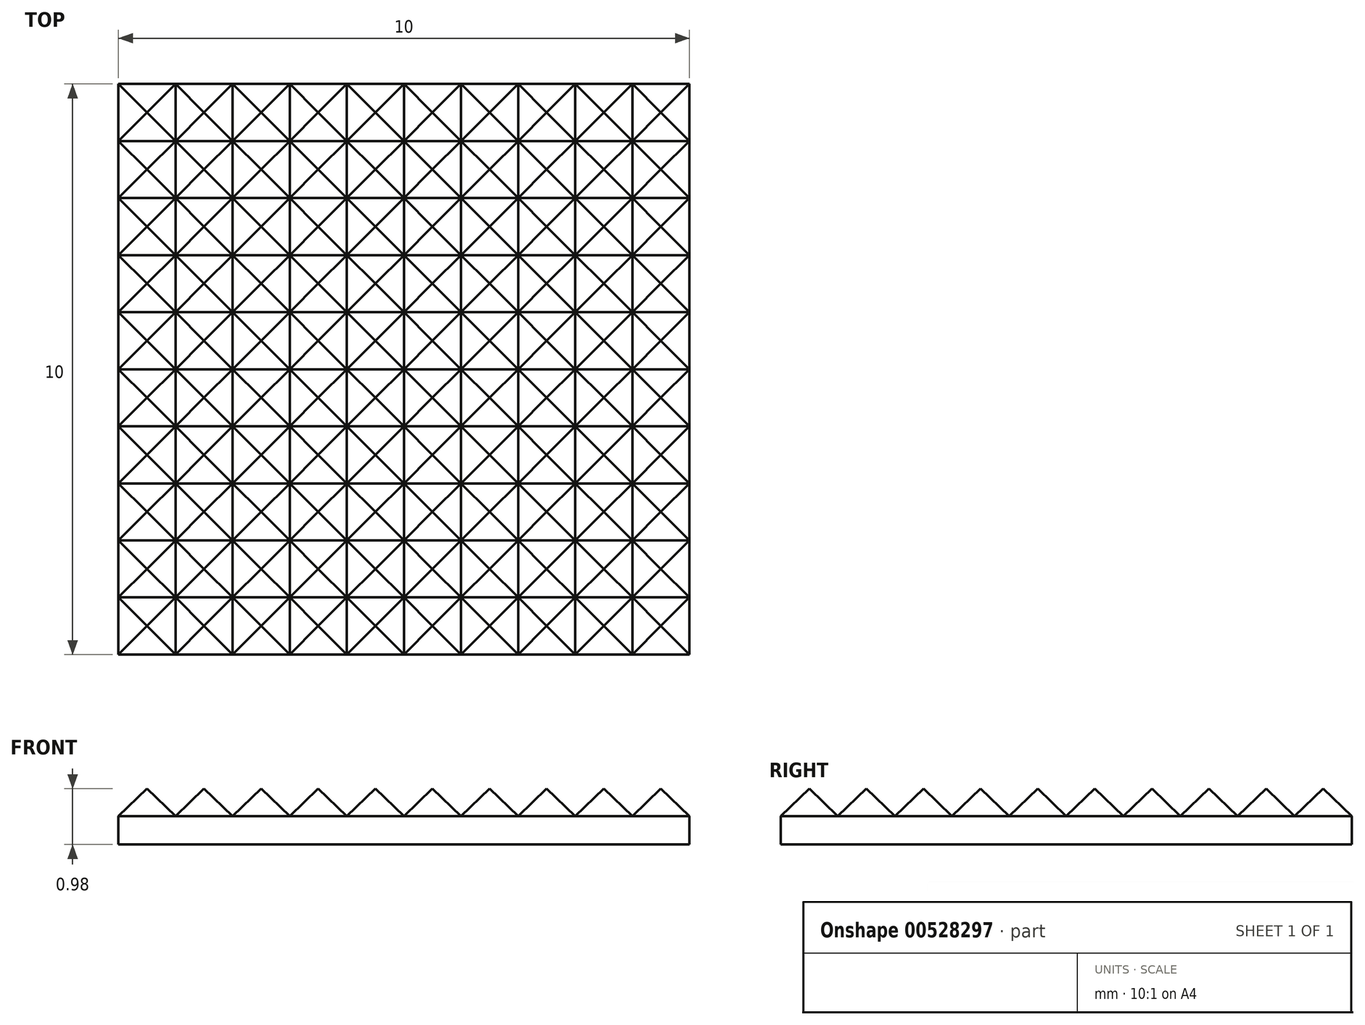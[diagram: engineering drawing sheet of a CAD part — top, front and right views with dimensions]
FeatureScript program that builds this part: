
annotation { "Feature Type Name" : "Feature", "Feature Type Description" : "" }
export const myFeature = defineFeature(function(context is Context, id is Id, definition is map)
    precondition{}
    {
        {
            var Q0;
            Q0=qCreatedBy(makeId("Top.planeOp"),FACE);
            var sketch = newSketch(context, id + "F0", { "sketchPlane" : qUnion([Q0])});
            skLineSegment(sketch, "E0.bottom", {"start": v(0, 0) * mm, "end": v(10, 0) * mm});
            skLineSegment(sketch, "E0.top", {"start": v(0, -10) * mm, "end": v(10, -10) * mm});
            skLineSegment(sketch, "E0.left", {"start": v(0, 0) * mm, "end": v(0, -10) * mm});
            skLineSegment(sketch, "E0.right", {"start": v(10, 0) * mm, "end": v(10, -10) * mm});
            skSolve(sketch);
        }
        {
            var Q0;
            Q0 = qSketchRegion(id + "F0", true);
            extrude(context, id + "F1", {"entities" : qUnion([Q0]), "depth" : 1 * mm, "offsetDistance" : 25 * mm});
        }
        {
            var Q0;
            Q0=makeQuery(id+"F1.opExtrude","SWEPT_FACE",FACE,{"disambiguationData":[OSD([sQuery(id+"F0.wireOp",EDGE,"E0.bottom")])]});
            var sketch = newSketch(context, id + "F2", { "sketchPlane" : qUnion([Q0])});
            skLineSegment(sketch, "E1", {"start": v(-10, 0.5) * mm, "end": v(0, 0.5) * mm});
            skLineSegment(sketch, "E2", {"start": v(0, 0.5) * mm, "end": v(-0.5, 0.98) * mm});
            skLineSegment(sketch, "E3", {"start": v(-0.5, 0.98) * mm, "end": v(-1, 0.5) * mm});
            skLineSegment(sketch, "E4.1.0.0", {"start": v(-1.5, 0.98) * mm, "end": v(-2, 0.5) * mm});
            skLineSegment(sketch, "E4.1.0.1", {"start": v(-1, 0.5) * mm, "end": v(-1.5, 0.98) * mm});
            skLineSegment(sketch, "E4.2.0.0", {"start": v(-2.5, 0.98) * mm, "end": v(-3, 0.5) * mm});
            skLineSegment(sketch, "E4.2.0.1", {"start": v(-2, 0.5) * mm, "end": v(-2.5, 0.98) * mm});
            skLineSegment(sketch, "E4.3.0.0", {"start": v(-3.5, 0.98) * mm, "end": v(-4, 0.5) * mm});
            skLineSegment(sketch, "E4.3.0.1", {"start": v(-3, 0.5) * mm, "end": v(-3.5, 0.98) * mm});
            skLineSegment(sketch, "E4.4.0.0", {"start": v(-4.5, 0.98) * mm, "end": v(-5, 0.5) * mm});
            skLineSegment(sketch, "E4.4.0.1", {"start": v(-4, 0.5) * mm, "end": v(-4.5, 0.98) * mm});
            skLineSegment(sketch, "E4.5.0.0", {"start": v(-5.5, 0.98) * mm, "end": v(-6, 0.5) * mm});
            skLineSegment(sketch, "E4.5.0.1", {"start": v(-5, 0.5) * mm, "end": v(-5.5, 0.98) * mm});
            skLineSegment(sketch, "E4.6.0.0", {"start": v(-6.5, 0.98) * mm, "end": v(-7, 0.5) * mm});
            skLineSegment(sketch, "E4.6.0.1", {"start": v(-6, 0.5) * mm, "end": v(-6.5, 0.98) * mm});
            skLineSegment(sketch, "E4.7.0.0", {"start": v(-7.5, 0.98) * mm, "end": v(-8, 0.5) * mm});
            skLineSegment(sketch, "E4.7.0.1", {"start": v(-7, 0.5) * mm, "end": v(-7.5, 0.98) * mm});
            skLineSegment(sketch, "E4.8.0.0", {"start": v(-8.5, 0.98) * mm, "end": v(-9, 0.5) * mm});
            skLineSegment(sketch, "E4.8.0.1", {"start": v(-8, 0.5) * mm, "end": v(-8.5, 0.98) * mm});
            skLineSegment(sketch, "E4.9.0.0", {"start": v(-9.5, 0.98) * mm, "end": v(-10, 0.5) * mm});
            skLineSegment(sketch, "E4.9.0.1", {"start": v(-9, 0.5) * mm, "end": v(-9.5, 0.98) * mm});
            skLineSegment(sketch, "E4.direction1", {"start": v(-1, 0.5) * mm, "end": v(-2, 0.5) * mm, "construction": true});
            skSolve(sketch);
        }
        {
            var Q0;
            Q0=makeQuery(id+"F1.opExtrude","SWEPT_FACE",FACE,{"disambiguationData":[OSD([sQuery(id+"F0.wireOp",EDGE,"E0.left")])]});
            var sketch = newSketch(context, id + "F3", { "sketchPlane" : qUnion([Q0])});
            skLineSegment(sketch, "E5", {"start": v(0, 0.5) * mm, "end": v(10, 0.5) * mm});
            skLineSegment(sketch, "E6", {"start": v(0, 0.5) * mm, "end": v(0.5, 0.98) * mm});
            skLineSegment(sketch, "E7", {"start": v(0.5, 0.98) * mm, "end": v(1, 0.5) * mm});
            skLineSegment(sketch, "E8.1.0.0", {"start": v(1, 0.5) * mm, "end": v(1.5, 0.98) * mm});
            skLineSegment(sketch, "E8.1.0.1", {"start": v(1.5, 0.98) * mm, "end": v(2, 0.5) * mm});
            skLineSegment(sketch, "E8.2.0.0", {"start": v(2, 0.5) * mm, "end": v(2.5, 0.98) * mm});
            skLineSegment(sketch, "E8.2.0.1", {"start": v(2.5, 0.98) * mm, "end": v(3, 0.5) * mm});
            skLineSegment(sketch, "E8.3.0.0", {"start": v(3, 0.5) * mm, "end": v(3.5, 0.98) * mm});
            skLineSegment(sketch, "E8.3.0.1", {"start": v(3.5, 0.98) * mm, "end": v(4, 0.5) * mm});
            skLineSegment(sketch, "E8.4.0.0", {"start": v(4, 0.5) * mm, "end": v(4.5, 0.98) * mm});
            skLineSegment(sketch, "E8.4.0.1", {"start": v(4.5, 0.98) * mm, "end": v(5, 0.5) * mm});
            skLineSegment(sketch, "E8.5.0.0", {"start": v(5, 0.5) * mm, "end": v(5.5, 0.98) * mm});
            skLineSegment(sketch, "E8.5.0.1", {"start": v(5.5, 0.98) * mm, "end": v(6, 0.5) * mm});
            skLineSegment(sketch, "E8.6.0.0", {"start": v(6, 0.5) * mm, "end": v(6.5, 0.98) * mm});
            skLineSegment(sketch, "E8.6.0.1", {"start": v(6.5, 0.98) * mm, "end": v(7, 0.5) * mm});
            skLineSegment(sketch, "E8.7.0.0", {"start": v(7, 0.5) * mm, "end": v(7.5, 0.98) * mm});
            skLineSegment(sketch, "E8.7.0.1", {"start": v(7.5, 0.98) * mm, "end": v(8, 0.5) * mm});
            skLineSegment(sketch, "E8.8.0.0", {"start": v(8, 0.5) * mm, "end": v(8.5, 0.98) * mm});
            skLineSegment(sketch, "E8.8.0.1", {"start": v(8.5, 0.98) * mm, "end": v(9, 0.5) * mm});
            skLineSegment(sketch, "E8.9.0.0", {"start": v(9, 0.5) * mm, "end": v(9.5, 0.98) * mm});
            skLineSegment(sketch, "E8.9.0.1", {"start": v(9.5, 0.98) * mm, "end": v(10, 0.5) * mm});
            skLineSegment(sketch, "E8.direction1", {"start": v(0, 0.5) * mm, "end": v(1, 0.5) * mm, "construction": true});
            skSolve(sketch);
        }
        {
            var Q0;
            {var subQ4=sQuery(id+"F3.wireOp",EDGE,"E6");Q0=makeQuery(id+"F3.imprint","IMPRINT",FACE,{"disambiguationData":[TD([[makeQuery(id+"F3.imprint","IMPRINT",EDGE,{"derivedFrom":subQ4}),1.0]])]});}
            extrude(context, id + "F4", {"entities" : qUnion([Q0]), "operationType" : NewBodyOperationType.REMOVE, "oppositeDirection" : true, "depth" : 25 * mm, "offsetDistance" : 25 * mm});
        }
        {
            var Q0;
            {var subQ4=sQuery(id+"F2.wireOp",EDGE,"E2");Q0=makeQuery(id+"F2.imprint","IMPRINT",FACE,{"disambiguationData":[TD([[makeQuery(id+"F2.imprint","IMPRINT",EDGE,{"derivedFrom":subQ4}),-1.0]])]});}
            extrude(context, id + "F5", {"entities" : qUnion([Q0]), "operationType" : NewBodyOperationType.REMOVE, "oppositeDirection" : true, "depth" : 25 * mm, "offsetDistance" : 25 * mm});
        }
    });
